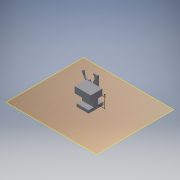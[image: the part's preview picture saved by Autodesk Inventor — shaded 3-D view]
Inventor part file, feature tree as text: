
AUTODESK INVENTOR PART (.ipt)
format: ipt  version: 2018 (Build 220112000, 112)  size: 210,432 bytes
history: native  units: mm
features: extrude x6, sketch x6, projected_geometry x6, other x4, plane x3, reference x1
ambient origin geometry x8: Origin, YZ Plane, XZ Plane, XY Plane, X Axis, Y Axis, Z Axis, Center Point
bodies: Solid1 (feature_tree)
feature tree (26):
  other  "Annotations"
  plane  "Work Plane1"
  plane  "Work Plane2"
  extrude  "Extrusion1"  Depth=15.0mm
  plane  "Work Plane3"
  extrude  "Extrusion2"  Depth=40.0mm
  extrude  "Extrusion3"  Depth=10.0mm TaperAngle=0.0deg
  extrude  "Extrusion4"  Depth=21.0mm
  extrude  "Extrusion5"  Depth=15.0mm
  extrude  "Extrusion6"  Depth=8.0mm
  sketch  "Sketch1"  dims[d0=40.0mm d1=15.0mm]
  reference  "Reference1"
  sketch  "Sketch2"  dims[d2=40.0mm d3=0.0mm d7=40.0mm]
  projected_geometry  "Projected Loop1"
  sketch  "Sketch3"  dims[d8=50.0mm d9=10.0mm d10=0.0mm]
  sketch  "Sketch4"  dims[d11=55.0mm d12=21.0mm]
  projected_geometry  "Projected Loop2"
  sketch  "Sketch5"  dims[d13=40.0mm d14=0.0mm d15=15.0mm]
  projected_geometry  "Projected Loop3"
  sketch  "Sketch6"  dims[d16=0.0mm d17=8.0mm d18=8.0mm d19=0.0mm d20=13.0mm d21=0.0mm d22=13.0mm d23=180.0deg d24=10.0mm d25=40.0mm d26=5.0mm d27=15.0mm d28=40.0mm d29=5.0mm d30=0.0mm d31=10.0mm d32=27.0mm d33=26.0mm d34=27.0mm d35=26.0mm d36=5.0mm d37=0.0mm d4=0.0mm d5=10.0mm d6=34.0mm]
  projected_geometry  "Projected Loop4"
  projected_geometry  "Projected Loop5"
  projected_geometry  "Projected Loop6"
  other  "Assembly1"
  other  "BSF_OuterFrame:1"
  other  "Linear Dimension 1"
